# Revit family: JC KONTAKTER JCK277 FI
name_source: partatom
category: Specialty Equipment
units: mm (PartAtom-declared; Revit-internal decimal feet)

## family parameters
Cut with Voids When Loaded = No
Enable Cutting in Views = Yes
Host = Face
Maintain Annotation Orientation = Yes
Part Type = Normal
Room Calculation Point = No
Round Connector Dimension = Use Diameter
Shared = No

## types (1)
- JCK277
    CE asiakirja = https://jckontakter.se
    Default Elevation = 800 mm  [stored 2.62467 ft]
    Description = Moderni malli varustettu ohjaavalla LED-valolla (sininen). Valmistettu mustasta eloksoidusta alumiinista mustalla päätykappaleella.
    Kansi = Aluminum ENAW 6060 (Musta)
    Kotelo = Aluminum ENAW 6060
    Linssi = Akryyli
    Manufacturer = JC Kontakter
    Mikrokytkimien määrä = 2
    Mikrokytkin = Standar NO IP67
    Model = JCK277
    Nimellisestä nimellisvirrasta = 12 V Resitiivinen 6A Induktiivinen L/R 5 ms 6A, 24 V Resistiivinen 6A Induktiivinen L/R 5 ms 5A
    Pienin nimellisvirta = 1mA/4 V DC
    Päätypäät = POM Tenac C 4520
    Tekniken tuotekortti = https://www.jckontakter.fi
    Tuotteen paino = 0.310 kg
    URL = https://www.jckontakter.fi
    Valmistusmaa = Ruotsi

note: [stored X ft] marks values corroborated as IEEE doubles in the binary element streams (Revit-internal decimal feet)

## geometry (parser evidence)
native form markers: Sweep x6
no freeform markers — native parametric forms only
